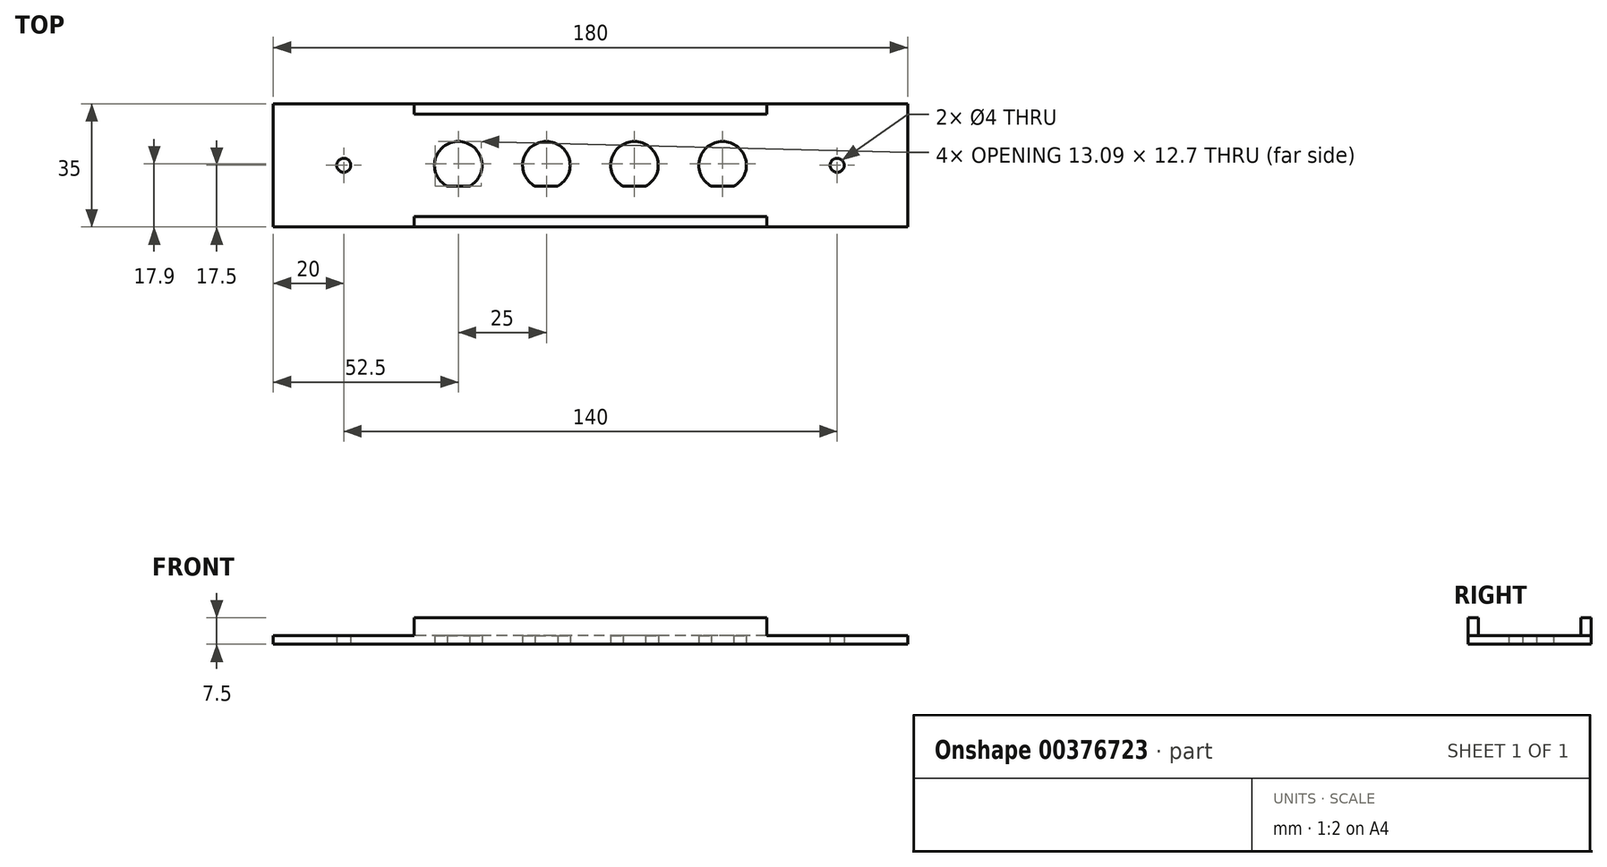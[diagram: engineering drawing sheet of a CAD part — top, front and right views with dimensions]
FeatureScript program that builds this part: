
annotation { "Feature Type Name" : "Feature", "Feature Type Description" : "" }
export const myFeature = defineFeature(function(context is Context, id is Id, definition is map)
    precondition{}
    {
        {
            var Q0;
            Q0=qCreatedBy(makeId("Top.planeOp"),FACE);
            var sketch = newSketch(context, id + "F0", { "sketchPlane" : qUnion([Q0])});
            skLineSegment(sketch, "E0.bottom", {"start": v(-90, 17.5) * mm, "end": v(90, 17.5) * mm});
            skLineSegment(sketch, "E0.top", {"start": v(-90, -17.5) * mm, "end": v(90, -17.5) * mm});
            skLineSegment(sketch, "E0.left", {"start": v(-90, 17.5) * mm, "end": v(-90, -17.5) * mm});
            skLineSegment(sketch, "E0.right", {"start": v(90, 17.5) * mm, "end": v(90, -17.5) * mm});
            skPoint(sketch, "E0.middle", {"position": v(0, 0) * mm});
            skCircle(sketch, "E1", {"center": v(-70, 0) * mm, "radius": 2 * mm});
            skCircle(sketch, "E2.MirrorC", {"center": v(70, 0) * mm, "radius": 2 * mm});
            skArc(sketch, "E3", {"start": v(-9.31, -5.95) * mm, "mid": v(-12.5, 6.75) * mm, "end": v(-15.69, -5.95) * mm});
            skLineSegment(sketch, "E4", {"start": v(-15.69, -5.95) * mm, "end": v(-9.31, -5.95) * mm});
            skPoint(sketch, "E5.center.orphan", {"position": v(-36.05, 0) * mm});
            skArc(sketch, "E6.1.0.0", {"start": v(-34.31, -5.95) * mm, "mid": v(-37.5, 6.75) * mm, "end": v(-40.69, -5.95) * mm});
            skLineSegment(sketch, "E7", {"start": v(-50, 27.08) * mm, "end": v(-50, -33.59) * mm, "construction": true});
            skArc(sketch, "E8.MirrorCS", {"start": v(9.31, -5.95) * mm, "mid": v(12.5, 6.75) * mm, "end": v(15.69, -5.95) * mm});
            skArc(sketch, "E9.MirrorCS", {"start": v(34.31, -5.95) * mm, "mid": v(37.5, 6.75) * mm, "end": v(40.69, -5.95) * mm});
            skLineSegment(sketch, "E10.MirrorCS", {"start": v(50, 27.08) * mm, "end": v(50, -33.59) * mm, "construction": true});
            skLineSegment(sketch, "E11.MirrorCS", {"start": v(15.69, -5.95) * mm, "end": v(9.31, -5.95) * mm});
            skLineSegment(sketch, "E12.1.0.0", {"start": v(-40.69, -5.95) * mm, "end": v(-34.31, -5.95) * mm});
            skLineSegment(sketch, "E13.MirrorCS", {"start": v(40.69, -5.95) * mm, "end": v(34.31, -5.95) * mm});
            skSolve(sketch);
        }
        {
            var Q0;
            Q0=makeQuery(id+"F0.imprint","IMPRINT",FACE,{"disambiguationData":[TD([[makeQuery(id+"F0.imprint","IMPRINT",EDGE,{"derivedFrom":sQuery(id+"F0.wireOp",EDGE,"E0.bottom")}),-1.0]])]});
            extrude(context, id + "F1", {"entities" : qUnion([Q0]), "depth" : 2.5 * mm});
        }
        {
            var Q0;
            Q0=makeQuery(id+"F1.opExtrude","CAP_FACE",FACE,{"disambiguationData":[OSD([sQuery(id+"F0.wireOp",EDGE,"E0.bottom"),sQuery(id+"F0.wireOp",EDGE,"E0.top"),sQuery(id+"F0.wireOp",EDGE,"E0.left"),sQuery(id+"F0.wireOp",EDGE,"E0.right"),sQuery(id+"F0.wireOp",EDGE,"E1"),sQuery(id+"F0.wireOp",EDGE,"E2.MirrorC"),sQuery(id+"F0.wireOp",EDGE,"E3"),sQuery(id+"F0.wireOp",EDGE,"E4"),sQuery(id+"F0.wireOp",EDGE,"E6.1.0.0"),sQuery(id+"F0.wireOp",EDGE,"E8.MirrorCS"),sQuery(id+"F0.wireOp",EDGE,"E9.MirrorCS"),sQuery(id+"F0.wireOp",EDGE,"E11.MirrorCS"),sQuery(id+"F0.wireOp",EDGE,"E12.1.0.0"),sQuery(id+"F0.wireOp",EDGE,"E13.MirrorCS")])],"isStart":false});
            var sketch = newSketch(context, id + "F2", { "sketchPlane" : qUnion([Q0])});
            skLineSegment(sketch, "E14.bottom", {"start": v(50, -17.5) * mm, "end": v(-50, -17.5) * mm});
            skLineSegment(sketch, "E14.top", {"start": v(50, -14.5) * mm, "end": v(-50, -14.5) * mm});
            skLineSegment(sketch, "E14.left", {"start": v(50, -17.5) * mm, "end": v(50, -14.5) * mm});
            skLineSegment(sketch, "E14.right", {"start": v(-50, -17.5) * mm, "end": v(-50, -14.5) * mm});
            skLineSegment(sketch, "E15.MirrorCS", {"start": v(-50, 17.5) * mm, "end": v(-50, 14.5) * mm});
            skLineSegment(sketch, "E16.MirrorCS", {"start": v(50, 17.5) * mm, "end": v(50, 14.5) * mm});
            skLineSegment(sketch, "E17.MirrorCS", {"start": v(50, 14.5) * mm, "end": v(-50, 14.5) * mm});
            skLineSegment(sketch, "E18.MirrorCS", {"start": v(50, 17.5) * mm, "end": v(-50, 17.5) * mm});
            skSolve(sketch);
        }
        {
            var Q0;
            Q0=makeQuery(id+"F2.imprint","IMPRINT",FACE,{"disambiguationData":[TD([[makeQuery(id+"F2.imprint","IMPRINT",EDGE,{"derivedFrom":sQuery(id+"F2.wireOp",EDGE,"E14.bottom")}),1.0]])]});
            var Q1;
            Q1=makeQuery(id+"F2.imprint","IMPRINT",FACE,{"disambiguationData":[TD([[makeQuery(id+"F2.imprint","IMPRINT",EDGE,{"derivedFrom":sQuery(id+"F2.wireOp",EDGE,"E15.MirrorCS")}),1.0]])]});
            extrude(context, id + "F3", {"entities" : qUnion([Q0, Q1]), "operationType" : NewBodyOperationType.ADD, "depth" : 5 * mm});
        }
    });
